# Revit family: ГРЕЕРС ЗВП-М2-200В
name_source: partatom
category: Оборудование
revit_build: Autodesk Revit 2017 (Build: 20161006_0315(x64)
units: mm (PartAtom-declared; Revit-internal decimal feet)

## family parameters
Всегда вертикально = Да
Заголовок OmniClass = Climate Control (HVAC)
На основе рабочей плоскости = Нет
Номер OmniClass = 23.75.00.00
Общий = Нет
При загрузке вырезать с полостями = Нет
Размер круглого соединителя = Использовать диаметр
Тип детали = Нормальный
Точка расчета площади = Нет

## types (1)
- ГРЕЕРС ЗВП-М2-200В
    URL = https://greers.ru
    Вентилятор = Осевой, однофазный, переменного тока, с 3-х скоростным двигателем, 3 шт.
    Вес аппарата = 82.00 кг
    Вес аппарата наполненного водой = 85.00 кг
    Группа модели = Воздушная завеса ЗВП-М2-200В
    Изготовитель = ООО "ЮНИО-ВЕНТ"
    Класс защиты = IP 54
    Классификация нагрузки = Двигатель
    Количество воды проходящей через теплообменник = 0.0 л/с
    Корпус вентилятора = Пластик
    Корпус завесы = Нержавеющая сталь
    Коэффициент мощности = 1
    Максимальное потребление тока = 0 А
    Напряжение питания = 230 В
    Описание = Промышленная воздушная завеса с водяным нагревом
    Падение давления воды в теплообменнике = 0.0 Па
    Патрубки = 20 мм
    Полная установленная мощность = 0 В·А
    Производительность = 0.0 м³/ч
    Температура воды на входе в аппарат = 0 °C
    Температура воды на выходе из теплооменника = 0 °C
    Температура воздуха на входе в аппарат = 0 °C
    Температура воздуха на выходе из аппарата = 0 °C
    Тепловая мощность = 0 кВт
